FCSTD DOCUMENT  (FreeCAD 0.19R)
Label: soleh
License: All rights reserved
LicenseURL: http://en.wikipedia.org/wiki/All_rights_reserved
objects: Sketcher::SketchObject×1, Part::FeaturePython×1
note: 2 computed .brp shape members not serialized (recipe doc carries the construction recipe); baked Part::Feature solids carry a one-line shape summary decoded from their .brp

FEATURE [Sketcher::SketchObject] Sketch
  FullyConstrained = true
  Placement = pos=(0,0,0) rot=(1,0,0;1.5708rad)
  sketch-geometry (7):
    g0: LineSegment StartX=0 StartY=0 StartZ=0 EndX=0 EndY=7600 EndZ=0
    g1: LineSegment StartX=0 StartY=7600 StartZ=0 EndX=12500 EndY=12149.6 EndZ=0
    g2: LineSegment StartX=12500 StartY=12149.6 StartZ=0 EndX=25000 EndY=7600 EndZ=0
    g3: LineSegment StartX=25000 StartY=7600 StartZ=0 EndX=25000 EndY=0 EndZ=0
    g4: LineSegment StartX=37500 StartY=12149.6 StartZ=0 EndX=25000 EndY=7600 EndZ=0
    g5: LineSegment StartX=50000 StartY=0 StartZ=0 EndX=50000 EndY=7600 EndZ=0
    g6: LineSegment StartX=50000 StartY=7600 StartZ=0 EndX=37500 EndY=12149.6 EndZ=0
  constraints (21):
    c: Vertical(g0)
    c: Coincident(g0,g1)
    c: Coincident(g1,g2)
    c: Coincident(g2,g3)
    c: Vertical(g3)
    c: DistanceY(g0,g0) = 7600
    c: Angle(g0,g1) = 1.91986
    c: Equal(g1,g2)
    c: Vertical(g5)
    c: Coincident(g5,g6)
    c: Coincident(g6,g4)
    c: Angle(g5,g6) = -1.91986
    c: Coincident(g0,g-1)
    c: Coincident(g2,g4)
    c: Equal(g4,g1)
    c: Equal(g6,g1)
    c: DistanceY(g3,g0) = 0
    c: DistanceY(g5,g0) = 0
    c: Equal(g3,g0)
    c: Equal(g5,g0)
    c: DistanceX(g0,g1) = 12500
FEATURE [Part::FeaturePython] Component001  label="IFCSoleh"  # Arch/BIM 135 (typed FeaturePython)
  Base = -> Sketch
  HorizontalArea = 0
  IfcData = attributes={"GlobalId": {"name": "GlobalId", "type": "IfcGloballyUniqueId", "is_enum": false, "enum_values": []}, "Description": {"... (+537 chars omitted),+1 more (map truncated)
  IfcType = 135
  MoveBase = false
  MoveWithHost = false
  PerimeterLength = 0
  PredefinedType = 0
  VerticalArea = 0
